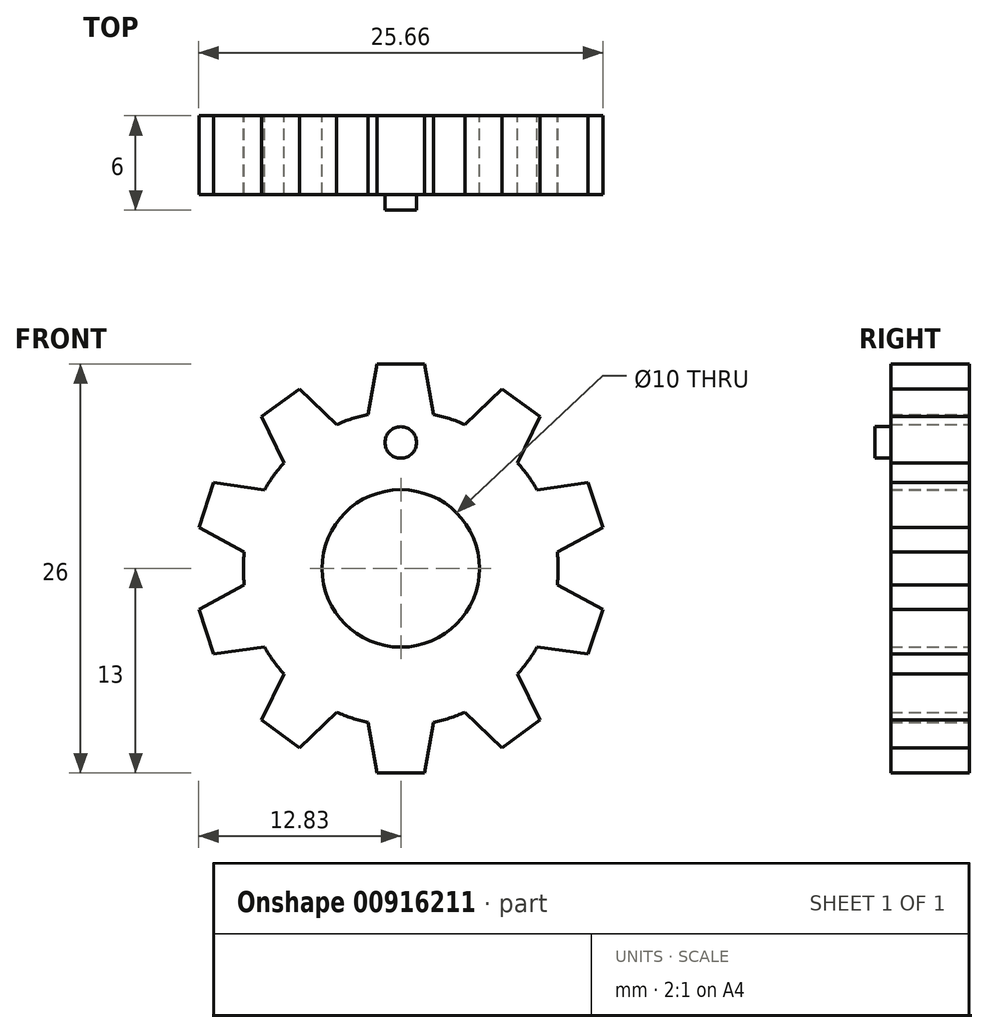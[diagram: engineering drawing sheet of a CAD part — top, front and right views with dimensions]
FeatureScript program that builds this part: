
annotation { "Feature Type Name" : "Feature", "Feature Type Description" : "" }
export const myFeature = defineFeature(function(context is Context, id is Id, definition is map)
    precondition{}
    {
        {
            var Q0;
            Q0=qCreatedBy(makeId("Front.planeOp"),FACE);
            var sketch = newSketch(context, id + "F0", { "sketchPlane" : qUnion([Q0])});
            skCircle(sketch, "E0", {"center": v(0, 0) * mm, "radius": 5 * mm});
            skCircle(sketch, "E1", {"center": v(0, 0) * mm, "radius": 10 * mm});
            skLineSegment(sketch, "E2", {"start": v(0, 13) * mm, "end": v(1.5, 13) * mm});
            skLineSegment(sketch, "E3", {"start": v(1.5, 13) * mm, "end": v(2.07, 9.78) * mm});
            skLineSegment(sketch, "E4.MirrorCS", {"start": v(0, 13) * mm, "end": v(-1.5, 13) * mm});
            skLineSegment(sketch, "E5.MirrorCS", {"start": v(-1.5, 13) * mm, "end": v(-2.07, 9.78) * mm});
            skLineSegment(sketch, "E6.1.0", {"start": v(-8.85, 9.64) * mm, "end": v(-7.42, 6.7) * mm});
            skLineSegment(sketch, "E6.1.1", {"start": v(-7.64, 10.52) * mm, "end": v(-8.85, 9.64) * mm});
            skLineSegment(sketch, "E6.1.2", {"start": v(-7.64, 10.52) * mm, "end": v(-6.43, 11.4) * mm});
            skLineSegment(sketch, "E6.1.3", {"start": v(-6.43, 11.4) * mm, "end": v(-4.08, 9.13) * mm});
            skLineSegment(sketch, "E6.2.0", {"start": v(-12.83, 2.6) * mm, "end": v(-9.94, 1.06) * mm});
            skLineSegment(sketch, "E6.2.1", {"start": v(-12.36, 4.02) * mm, "end": v(-12.83, 2.6) * mm});
            skLineSegment(sketch, "E6.2.2", {"start": v(-12.36, 4.02) * mm, "end": v(-11.9, 5.44) * mm});
            skLineSegment(sketch, "E6.2.3", {"start": v(-11.9, 5.44) * mm, "end": v(-8.67, 4.99) * mm});
            skLineSegment(sketch, "E7.2.3.0", {"start": v(-11.9, -5.44) * mm, "end": v(-8.67, -4.99) * mm});
            skLineSegment(sketch, "E7.3.3.0", {"start": v(-12.36, -4.02) * mm, "end": v(-11.9, -5.44) * mm});
            skLineSegment(sketch, "E7.6.3.0", {"start": v(-12.36, -4.02) * mm, "end": v(-12.83, -2.6) * mm});
            skLineSegment(sketch, "E7.9.3.0", {"start": v(-12.83, -2.6) * mm, "end": v(-9.94, -1.06) * mm});
            skLineSegment(sketch, "E7.2.4.0", {"start": v(-6.43, -11.4) * mm, "end": v(-4.08, -9.13) * mm});
            skLineSegment(sketch, "E7.3.4.0", {"start": v(-7.64, -10.52) * mm, "end": v(-6.43, -11.4) * mm});
            skLineSegment(sketch, "E7.6.4.0", {"start": v(-7.64, -10.52) * mm, "end": v(-8.85, -9.64) * mm});
            skLineSegment(sketch, "E7.9.4.0", {"start": v(-8.85, -9.64) * mm, "end": v(-7.42, -6.7) * mm});
            skLineSegment(sketch, "E7.2.5.0", {"start": v(1.5, -13) * mm, "end": v(2.07, -9.78) * mm});
            skLineSegment(sketch, "E7.3.5.0", {"start": v(0, -13) * mm, "end": v(1.5, -13) * mm});
            skLineSegment(sketch, "E7.6.5.0", {"start": v(0, -13) * mm, "end": v(-1.5, -13) * mm});
            skLineSegment(sketch, "E7.9.5.0", {"start": v(-1.5, -13) * mm, "end": v(-2.07, -9.78) * mm});
            skLineSegment(sketch, "E7.2.6.0", {"start": v(8.85, -9.64) * mm, "end": v(7.42, -6.7) * mm});
            skLineSegment(sketch, "E7.3.6.0", {"start": v(7.64, -10.52) * mm, "end": v(8.85, -9.64) * mm});
            skLineSegment(sketch, "E7.6.6.0", {"start": v(7.64, -10.52) * mm, "end": v(6.43, -11.4) * mm});
            skLineSegment(sketch, "E7.9.6.0", {"start": v(6.43, -11.4) * mm, "end": v(4.08, -9.13) * mm});
            skLineSegment(sketch, "E7.2.7.0", {"start": v(12.83, -2.6) * mm, "end": v(9.94, -1.06) * mm});
            skLineSegment(sketch, "E7.3.7.0", {"start": v(12.36, -4.02) * mm, "end": v(12.83, -2.6) * mm});
            skLineSegment(sketch, "E7.6.7.0", {"start": v(12.36, -4.02) * mm, "end": v(11.9, -5.44) * mm});
            skLineSegment(sketch, "E7.9.7.0", {"start": v(11.9, -5.44) * mm, "end": v(8.67, -4.99) * mm});
            skLineSegment(sketch, "E7.2.8.0", {"start": v(11.9, 5.44) * mm, "end": v(8.67, 4.99) * mm});
            skLineSegment(sketch, "E7.3.8.0", {"start": v(12.36, 4.02) * mm, "end": v(11.9, 5.44) * mm});
            skLineSegment(sketch, "E7.6.8.0", {"start": v(12.36, 4.02) * mm, "end": v(12.83, 2.6) * mm});
            skLineSegment(sketch, "E7.9.8.0", {"start": v(12.83, 2.6) * mm, "end": v(9.94, 1.06) * mm});
            skLineSegment(sketch, "E7.2.9.0", {"start": v(6.43, 11.4) * mm, "end": v(4.08, 9.13) * mm});
            skLineSegment(sketch, "E7.3.9.0", {"start": v(7.64, 10.52) * mm, "end": v(6.43, 11.4) * mm});
            skLineSegment(sketch, "E7.6.9.0", {"start": v(7.64, 10.52) * mm, "end": v(8.85, 9.64) * mm});
            skLineSegment(sketch, "E7.9.9.0", {"start": v(8.85, 9.64) * mm, "end": v(7.42, 6.7) * mm});
            skSolve(sketch);
        }
        {
            var Q0;
            Q0 = qSketchRegion(id + "F0", true);
            extrude(context, id + "F1", {"entities" : qUnion([Q0]), "depth" : 5 * mm, "offsetDistance" : 25 * mm});
        }
        {
            var Q0;
            Q0=makeQuery(id+"F1.opExtrude","CAP_FACE",FACE,{"disambiguationData":[OSD([sQuery(id+"F0.wireOp",EDGE,"E0"),sQuery(id+"F0.wireOp",EDGE,"E1"),sQuery(id+"F0.wireOp",EDGE,"E2"),sQuery(id+"F0.wireOp",EDGE,"E3"),sQuery(id+"F0.wireOp",EDGE,"E4.MirrorCS"),sQuery(id+"F0.wireOp",EDGE,"E5.MirrorCS"),sQuery(id+"F0.wireOp",EDGE,"E6.1.0"),sQuery(id+"F0.wireOp",EDGE,"E6.1.1"),sQuery(id+"F0.wireOp",EDGE,"E6.1.2"),sQuery(id+"F0.wireOp",EDGE,"E6.1.3"),sQuery(id+"F0.wireOp",EDGE,"E6.2.0"),sQuery(id+"F0.wireOp",EDGE,"E6.2.1"),sQuery(id+"F0.wireOp",EDGE,"E6.2.2"),sQuery(id+"F0.wireOp",EDGE,"E6.2.3"),sQuery(id+"F0.wireOp",EDGE,"E7.2.3.0"),sQuery(id+"F0.wireOp",EDGE,"E7.3.3.0"),sQuery(id+"F0.wireOp",EDGE,"E7.6.3.0"),sQuery(id+"F0.wireOp",EDGE,"E7.9.3.0"),sQuery(id+"F0.wireOp",EDGE,"E7.2.4.0"),sQuery(id+"F0.wireOp",EDGE,"E7.3.4.0"),sQuery(id+"F0.wireOp",EDGE,"E7.6.4.0"),sQuery(id+"F0.wireOp",EDGE,"E7.9.4.0"),sQuery(id+"F0.wireOp",EDGE,"E7.2.5.0"),sQuery(id+"F0.wireOp",EDGE,"E7.3.5.0"),sQuery(id+"F0.wireOp",EDGE,"E7.6.5.0"),sQuery(id+"F0.wireOp",EDGE,"E7.9.5.0"),sQuery(id+"F0.wireOp",EDGE,"E7.2.6.0"),sQuery(id+"F0.wireOp",EDGE,"E7.3.6.0"),sQuery(id+"F0.wireOp",EDGE,"E7.6.6.0"),sQuery(id+"F0.wireOp",EDGE,"E7.9.6.0"),sQuery(id+"F0.wireOp",EDGE,"E7.2.7.0"),sQuery(id+"F0.wireOp",EDGE,"E7.3.7.0"),sQuery(id+"F0.wireOp",EDGE,"E7.6.7.0"),sQuery(id+"F0.wireOp",EDGE,"E7.9.7.0"),sQuery(id+"F0.wireOp",EDGE,"E7.2.8.0"),sQuery(id+"F0.wireOp",EDGE,"E7.3.8.0"),sQuery(id+"F0.wireOp",EDGE,"E7.6.8.0"),sQuery(id+"F0.wireOp",EDGE,"E7.9.8.0"),sQuery(id+"F0.wireOp",EDGE,"E7.2.9.0"),sQuery(id+"F0.wireOp",EDGE,"E7.3.9.0"),sQuery(id+"F0.wireOp",EDGE,"E7.6.9.0"),sQuery(id+"F0.wireOp",EDGE,"E7.9.9.0")])],"isStart":false});
            var sketch = newSketch(context, id + "F2", { "sketchPlane" : qUnion([Q0])});
            skCircle(sketch, "E8", {"center": v(0, 8) * mm, "radius": 1 * mm});
            skSolve(sketch);
        }
        {
            var Q0;
            Q0 = qSketchRegion(id + "F2", true);
            extrude(context, id + "F3", {"entities" : qUnion([Q0]), "operationType" : NewBodyOperationType.ADD, "depth" : 1 * mm, "offsetDistance" : 25 * mm});
        }
    });
